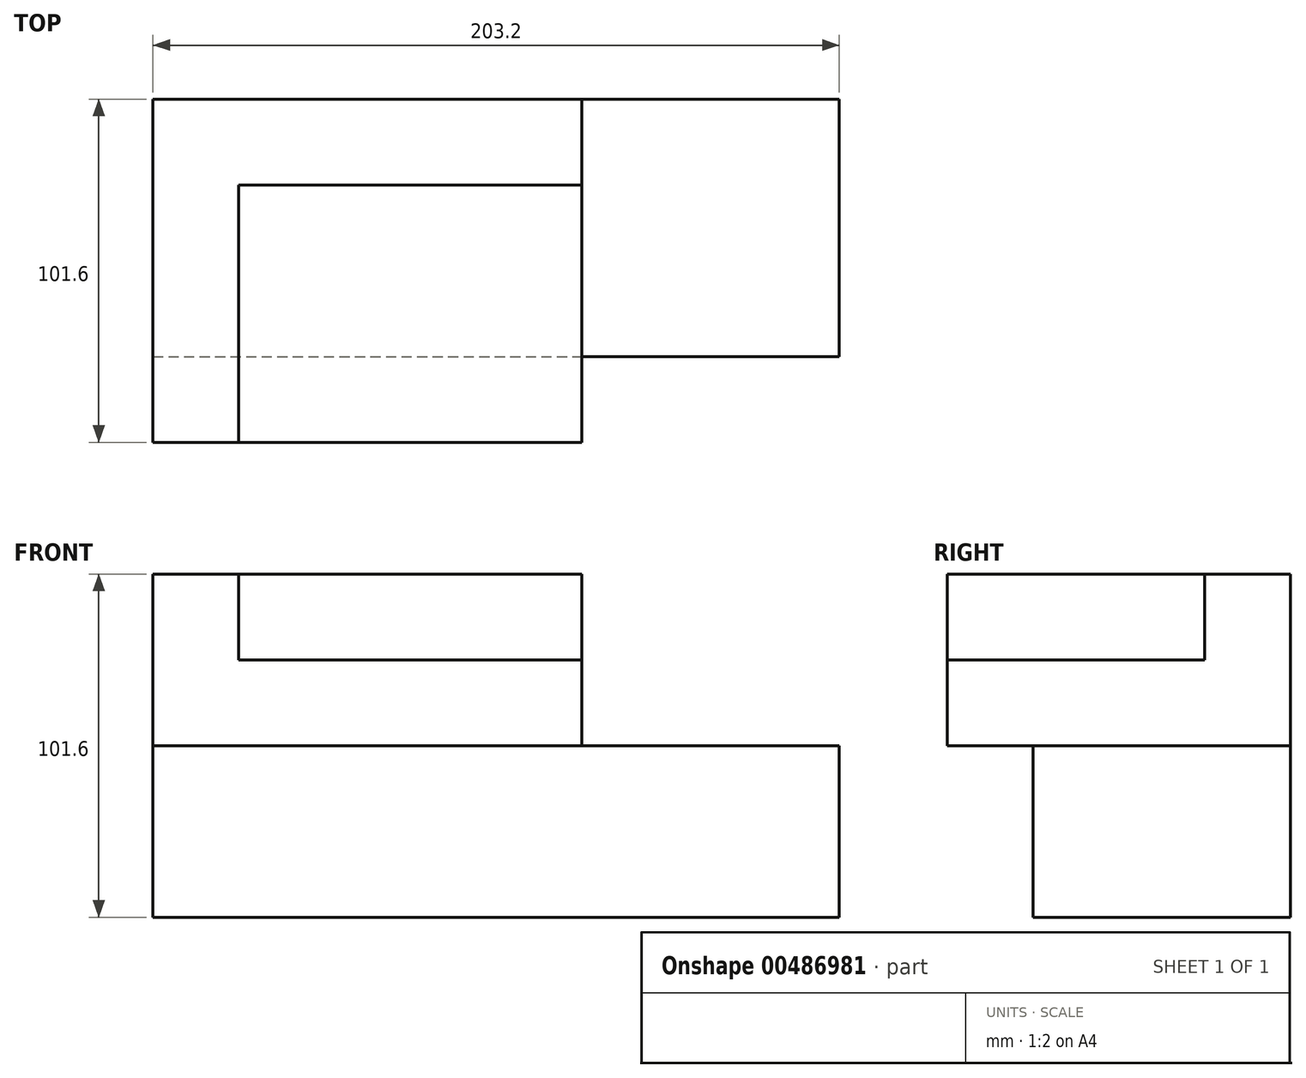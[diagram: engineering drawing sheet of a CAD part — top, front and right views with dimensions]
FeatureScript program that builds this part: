
annotation { "Feature Type Name" : "Feature", "Feature Type Description" : "" }
export const myFeature = defineFeature(function(context is Context, id is Id, definition is map)
    precondition{}
    {
        {
            var Q0;
            Q0=qCreatedBy(makeId("Front.planeOp"),FACE);
            var sketch = newSketch(context, id + "F0", { "sketchPlane" : qUnion([Q0])});
            skLineSegment(sketch, "E0.bottom", {"start": v(-164.2, -69.72) * mm, "end": v(39, -69.72) * mm});
            skLineSegment(sketch, "E0.top", {"start": v(-164.2, -18.92) * mm, "end": v(39, -18.92) * mm});
            skLineSegment(sketch, "E0.left", {"start": v(-164.2, -69.72) * mm, "end": v(-164.2, -18.92) * mm});
            skLineSegment(sketch, "E0.right", {"start": v(39, -69.72) * mm, "end": v(39, -18.92) * mm});
            skSolve(sketch);
        }
        {
            var Q0;
            Q0 = qSketchRegion(id + "F0", true);
            extrude(context, id + "F1", {"entities" : qUnion([Q0]), "depth" : 76.2 * mm});
        }
        {
            var Q0;
            Q0=qCreatedBy(makeId("Front.planeOp"),FACE);
            var sketch = newSketch(context, id + "F2", { "sketchPlane" : qUnion([Q0])});
            skLineSegment(sketch, "E1.bottom", {"start": v(-164.2, -18.92) * mm, "end": v(-37.2, -18.92) * mm});
            skLineSegment(sketch, "E1.top", {"start": v(-164.2, 31.88) * mm, "end": v(-37.2, 31.88) * mm});
            skLineSegment(sketch, "E1.left", {"start": v(-164.2, -18.92) * mm, "end": v(-164.2, 31.88) * mm});
            skLineSegment(sketch, "E1.right", {"start": v(-37.2, -18.92) * mm, "end": v(-37.2, 31.88) * mm});
            skSolve(sketch);
        }
        {
            var Q0;
            Q0 = qSketchRegion(id + "F2", true);
            extrude(context, id + "F3", {"entities" : qUnion([Q0]), "operationType" : NewBodyOperationType.ADD, "depth" : 101.6 * mm});
        }
        {
            var Q0;
            Q0=makeQuery(id+"F3.opExtrude","CAP_FACE",FACE,{"disambiguationData":[OSD([sQuery(id+"F2.wireOp",EDGE,"E1.bottom"),sQuery(id+"F2.wireOp",EDGE,"E1.top"),sQuery(id+"F2.wireOp",EDGE,"E1.left"),sQuery(id+"F2.wireOp",EDGE,"E1.right")])],"isStart":false});
            var sketch = newSketch(context, id + "F4", { "sketchPlane" : qUnion([Q0])});
            skLineSegment(sketch, "E2.bottom", {"start": v(-37.2, 31.88) * mm, "end": v(-138.8, 31.88) * mm});
            skLineSegment(sketch, "E2.top", {"start": v(-37.2, 6.48) * mm, "end": v(-138.8, 6.48) * mm});
            skLineSegment(sketch, "E2.left", {"start": v(-37.2, 31.88) * mm, "end": v(-37.2, 6.48) * mm});
            skLineSegment(sketch, "E2.right", {"start": v(-138.8, 31.88) * mm, "end": v(-138.8, 6.48) * mm});
            skSolve(sketch);
        }
        {
            var Q0;
            Q0 = qSketchRegion(id + "F4", true);
            extrude(context, id + "F5", {"entities" : qUnion([Q0]), "operationType" : NewBodyOperationType.REMOVE, "oppositeDirection" : true, "depth" : 76.2 * mm});
        }
    });
